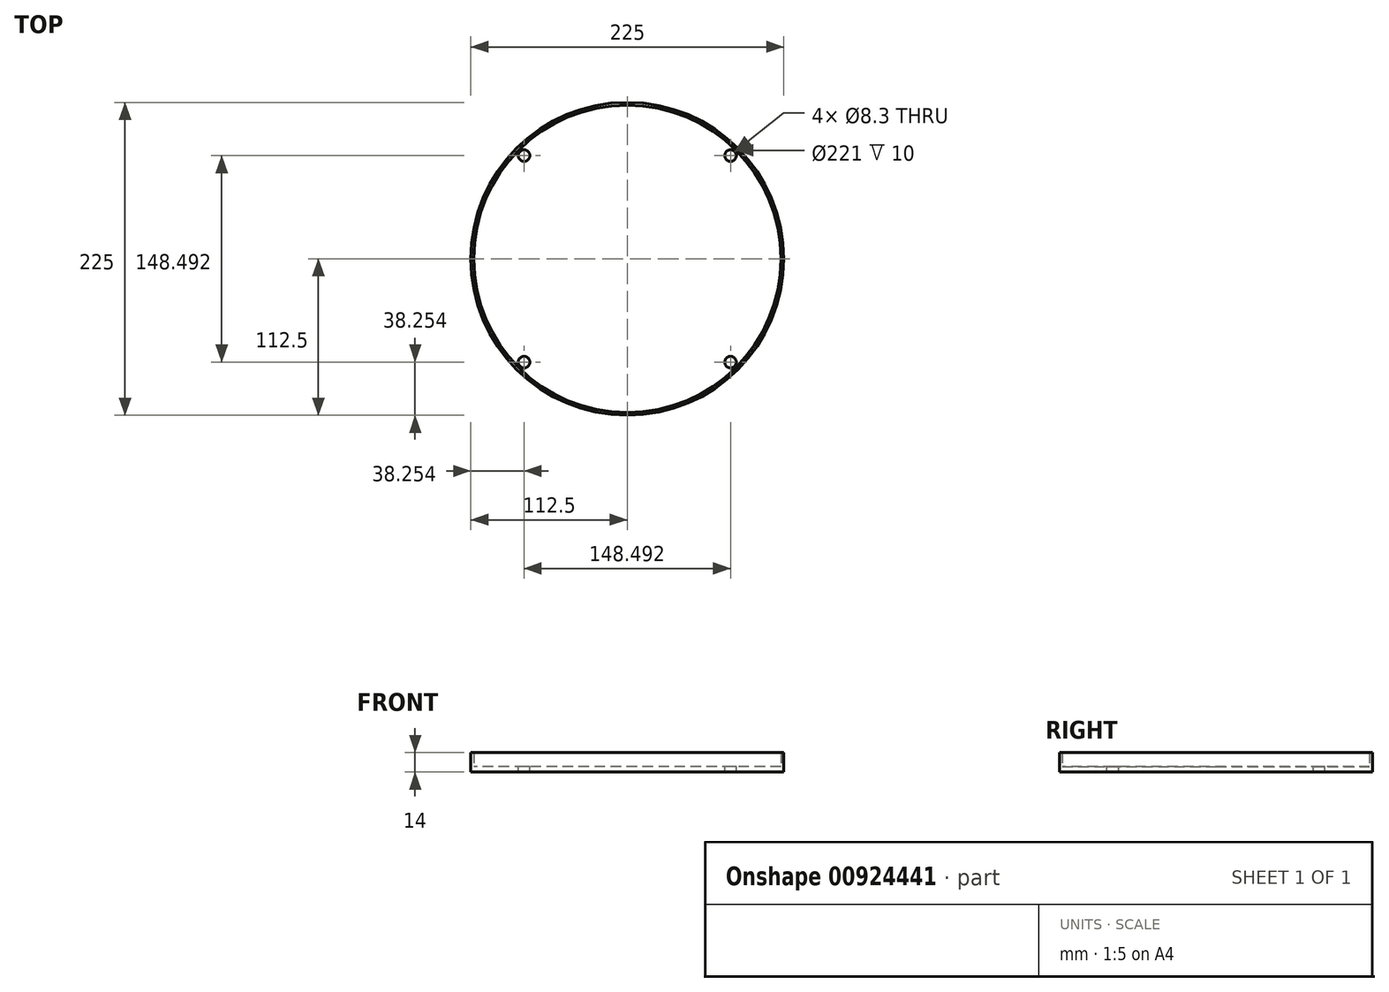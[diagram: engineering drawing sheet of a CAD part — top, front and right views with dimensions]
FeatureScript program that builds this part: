
annotation { "Feature Type Name" : "Feature", "Feature Type Description" : "" }
export const myFeature = defineFeature(function(context is Context, id is Id, definition is map)
    precondition{}
    {
        {
            var Q0;
            Q0=qCreatedBy(makeId("Top.planeOp"),FACE);
            var sketch = newSketch(context, id + "F0", { "sketchPlane" : qUnion([Q0])});
            skCircle(sketch, "E0", {"center": v(0, 0) * mm, "radius": 112.5 * mm});
            skSolve(sketch);
        }
        {
            var Q0;
            Q0=qSketchRegion(id+"F0",true);
            extrude(context, id + "F1", {"entities" : qUnion([Q0]), "depth" : 4 * mm, "offsetDistance" : 25 * mm});
        }
        {
            var Q0;
            Q0=makeQuery(id+"F1.opExtrude","CAP_FACE",FACE,{"disambiguationData":[OSD([sQuery(id+"F0.wireOp",EDGE,"E0")])],"isStart":false});
            var sketch = newSketch(context, id + "F2", { "sketchPlane" : qUnion([Q0])});
            skPoint(sketch, "E1", {"position": v(-74.25, 74.25) * mm});
            skPoint(sketch, "E2", {"position": v(74.25, 74.25) * mm});
            skPoint(sketch, "E3", {"position": v(-74.25, -74.25) * mm});
            skPoint(sketch, "E4", {"position": v(74.25, -74.25) * mm});
            skCircle(sketch, "E5", {"center": v(-74.25, 74.25) * mm, "radius": 4.15 * mm});
            skCircle(sketch, "E6", {"center": v(74.25, 74.25) * mm, "radius": 4.15 * mm});
            skCircle(sketch, "E7", {"center": v(74.25, -74.25) * mm, "radius": 4.15 * mm});
            skCircle(sketch, "E8", {"center": v(-74.25, -74.25) * mm, "radius": 4.15 * mm});
            skSolve(sketch);
        }
        {
            var Q0;
            Q0=makeQuery(id+"F2.imprint","IMPRINT",FACE,{"disambiguationData":[TD([[makeQuery(id+"F2.imprint","IMPRINT",EDGE,{"derivedFrom":sQuery(id+"F2.wireOp",EDGE,"E5")}),1.0]])]});
            var Q1;
            Q1=makeQuery(id+"F2.imprint","IMPRINT",FACE,{"disambiguationData":[TD([[makeQuery(id+"F2.imprint","IMPRINT",EDGE,{"derivedFrom":sQuery(id+"F2.wireOp",EDGE,"E8")}),1.0]])]});
            var Q2;
            Q2=makeQuery(id+"F2.imprint","IMPRINT",FACE,{"disambiguationData":[TD([[makeQuery(id+"F2.imprint","IMPRINT",EDGE,{"derivedFrom":sQuery(id+"F2.wireOp",EDGE,"E7")}),1.0]])]});
            var Q3;
            Q3=makeQuery(id+"F2.imprint","IMPRINT",FACE,{"disambiguationData":[TD([[makeQuery(id+"F2.imprint","IMPRINT",EDGE,{"derivedFrom":sQuery(id+"F2.wireOp",EDGE,"E6")}),1.0]])]});
            extrude(context, id + "F3", {"entities" : qUnion([Q0, Q1, Q2, Q3]), "operationType" : NewBodyOperationType.REMOVE, "oppositeDirection" : true, "depth" : 25 * mm, "offsetDistance" : 25 * mm});
        }
        {
            var Q0;
            Q0=makeQuery(id+"F1.opExtrude","CAP_FACE",FACE,{"disambiguationData":[OSD([sQuery(id+"F0.wireOp",EDGE,"E0")])],"isStart":false});
            var sketch = newSketch(context, id + "F4", { "sketchPlane" : qUnion([Q0])});
            skCircle(sketch, "E9", {"center": v(0, 0) * mm, "radius": 112.5 * mm});
            skCircle(sketch, "E10", {"center": v(0, 0) * mm, "radius": 110.5 * mm});
            skSolve(sketch);
        }
        {
            var Q0;
            Q0=makeQuery(id+"F4.imprint","IMPRINT",FACE,{"disambiguationData":[TD([[makeQuery(id+"F4.imprint","IMPRINT",EDGE,{"derivedFrom":sQuery(id+"F4.wireOp",EDGE,"E9")}),1.0]])]});
            extrude(context, id + "F5", {"entities" : qUnion([Q0]), "operationType" : NewBodyOperationType.ADD, "depth" : 10 * mm, "offsetDistance" : 25 * mm});
        }
    });
